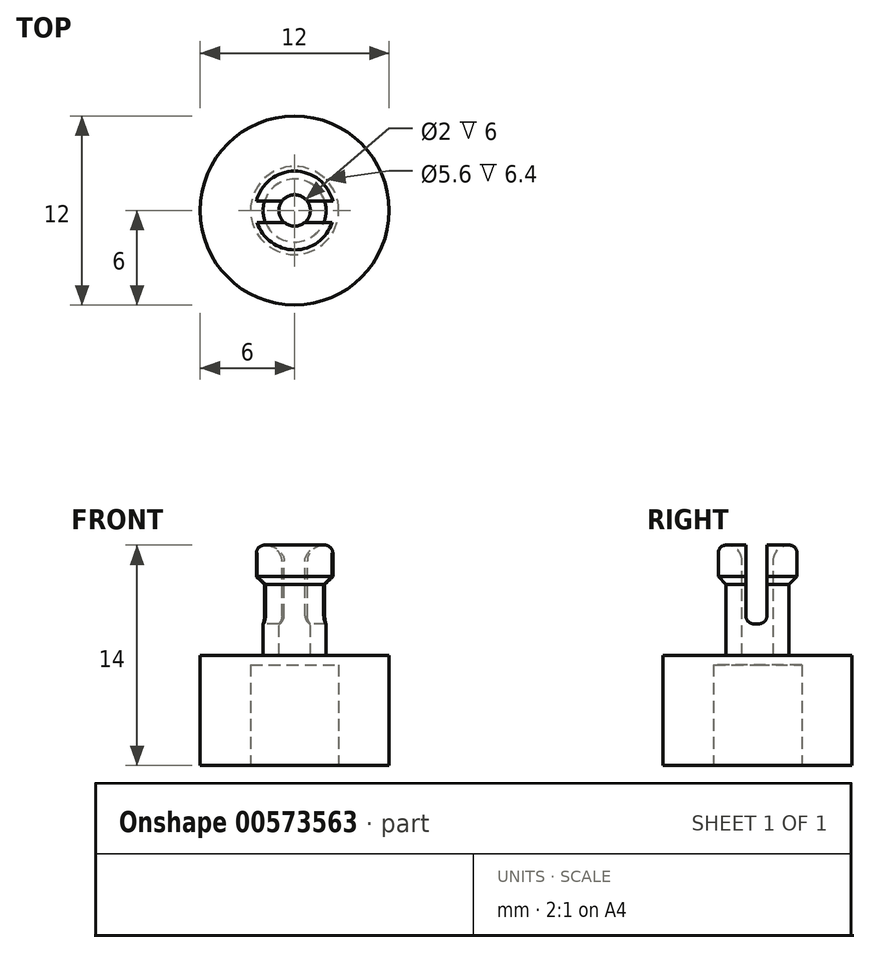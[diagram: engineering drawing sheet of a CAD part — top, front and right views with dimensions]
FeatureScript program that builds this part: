
annotation { "Feature Type Name" : "Feature", "Feature Type Description" : "" }
export const myFeature = defineFeature(function(context is Context, id is Id, definition is map)
    precondition{}
    {
        {
            var Q0;
            Q0=qCreatedBy(makeId("Right.planeOp"),FACE);
            var sketch = newSketch(context, id + "F0", { "sketchPlane" : qUnion([Q0])});
            skLineSegment(sketch, "E0", {"start": v(0, 0) * mm, "end": v(-6, 0) * mm});
            skLineSegment(sketch, "E1", {"start": v(-6, 0) * mm, "end": v(-6, 12) * mm});
            skLineSegment(sketch, "E2", {"start": v(-6, 12) * mm, "end": v(-2, 12) * mm});
            skPoint(sketch, "E3.end.orphan", {"position": v(0, 12) * mm});
            skLineSegment(sketch, "E4", {"start": v(-2, 12) * mm, "end": v(-2, 16) * mm});
            skLineSegment(sketch, "E5", {"start": v(-2, 19) * mm, "end": v(-1, 19) * mm});
            skLineSegment(sketch, "E6", {"start": v(0, 12) * mm, "end": v(0, 0) * mm});
            skLineSegment(sketch, "E7", {"start": v(-2, 16) * mm, "end": v(-2.5, 16) * mm});
            skLineSegment(sketch, "E8", {"start": v(-2.5, 16) * mm, "end": v(-2.5, 19) * mm});
            skLineSegment(sketch, "E9", {"start": v(-2.5, 19) * mm, "end": v(-2, 19) * mm});
            skLineSegment(sketch, "E10", {"start": v(0, 12) * mm, "end": v(-1, 12) * mm});
            skLineSegment(sketch, "E11", {"start": v(-1, 12) * mm, "end": v(-1, 16) * mm});
            skLineSegment(sketch, "E12", {"start": v(-1, 16) * mm, "end": v(-1, 19) * mm});
            skPoint(sketch, "E13.orphan", {"position": v(0, 19) * mm});
            skSolve(sketch);
        }
        {
            var Q0;
            Q0 = qSketchRegion(id + "F0", true);
            var Q1;
            Q1=sQuery(id+"F0.wireOp",EDGE,"E6");
            revolve(context, id + "F1", {"entities" : qUnion([Q0]), "axis" : qUnion([Q1]), "revolveType" : RevolveType.FULL});
        }
        {
            var Q0;
            Q0=makeQuery(id+"F1.opRevolve","SWEPT_FACE",FACE,{"disambiguationData":[OSD([sQuery(id+"F0.wireOp",EDGE,"E5"),sQuery(id+"F0.wireOp",EDGE,"E9")])]});
            var sketch = newSketch(context, id + "F2", { "sketchPlane" : qUnion([Q0])});
            skLineSegment(sketch, "E14", {"start": v(6.48, 0.6) * mm, "end": v(-2.43, 0.6) * mm});
            skLineSegment(sketch, "E15", {"start": v(-2.43, 0.6) * mm, "end": v(-2.63, 0.6) * mm});
            skLineSegment(sketch, "E16", {"start": v(-2.63, 0.6) * mm, "end": v(-2.63, -0.25) * mm});
            skLineSegment(sketch, "E17", {"start": v(6.6, -0.25) * mm, "end": v(6.6, 0.6) * mm});
            skLineSegment(sketch, "E18", {"start": v(6.6, 0.6) * mm, "end": v(2.43, 0.6) * mm});
            skLineSegment(sketch, "E19.MirrorCS", {"start": v(-4.62, -0.56) * mm, "end": v(-4.62, 0) * mm});
            skLineSegment(sketch, "E20.MirrorCS", {"start": v(4.46, -0.75) * mm, "end": v(-4.5, -0.75) * mm});
            skLineSegment(sketch, "E21.MirrorCS", {"start": v(-4.47, -0.56) * mm, "end": v(-4.62, -0.56) * mm});
            skLineSegment(sketch, "E22.MirrorCS", {"start": v(4.61, 0) * mm, "end": v(4.61, -0.56) * mm});
            skLineSegment(sketch, "E23.MirrorCS", {"start": v(4.61, -0.56) * mm, "end": v(4.47, -0.56) * mm});
            skPoint(sketch, "E24.end.orphan", {"position": v(-2.43, -0.25) * mm});
            skPoint(sketch, "E25.orphan", {"position": v(-4.62, 0) * mm});
            skPoint(sketch, "E26.MirrorCS.end.orphan", {"position": v(-4.47, 0) * mm});
            skPoint(sketch, "E26.MirrorCS.start.orphan", {"position": v(-2.5, 0) * mm});
            skPoint(sketch, "E27.start.orphan", {"position": v(2.49, -0.25) * mm});
            skSolve(sketch);
        }
        {
            var Q0;
            {var subQ0=sQuery(id+"F2.wireOp",EDGE,"E14");var subQ3=makeQuery(id+"F1.opRevolve","SWEPT_EDGE",EDGE,{"disambiguationData":[OSD([sQuery(id+"F0.wireOp",EDGE,"E5"),sQuery(id+"F0.wireOp",EDGE,"E12")])]});var subQ4=makeQuery(id+"F2.imprint","INTERSECT",VERTEX,{"disambiguationData":[OD(1.0)],"derivedFrom":[subQ3,subQ0]});Q0=makeQuery(id+"F2.imprint","IMPRINT",FACE,{"disambiguationData":[TD([[makeQuery(id+"F2.imprint","IMPRINT",EDGE,{"disambiguationData":[TD([[subQ4,-1.0]])],"derivedFrom":subQ0}),1.0]])]});}
            var Q1;
            {var subQ0=sQuery(id+"F2.wireOp",EDGE,"E14");var subQ1=makeQuery(id+"F1.opRevolve","SWEPT_EDGE",EDGE,{"disambiguationData":[OSD([sQuery(id+"F0.wireOp",EDGE,"E5"),sQuery(id+"F0.wireOp",EDGE,"E12")])]});var subQ2=makeQuery(id+"F2.imprint","INTERSECT",VERTEX,{"disambiguationData":[OD(0.0)],"derivedFrom":[subQ1,subQ0]});Q1=makeQuery(id+"F2.imprint","IMPRINT",FACE,{"disambiguationData":[TD([[makeQuery(id+"F2.imprint","IMPRINT",EDGE,{"disambiguationData":[TD([[subQ2,-1.0]])],"derivedFrom":subQ0}),1.0]])]});}
            var Q2;
            {var subQ0=sQuery(id+"F2.wireOp",EDGE,"E14");var subQ3=makeQuery(id+"F1.opRevolve","SWEPT_EDGE",EDGE,{"disambiguationData":[OSD([sQuery(id+"F0.wireOp",EDGE,"E5"),sQuery(id+"F0.wireOp",EDGE,"E12")])]});var subQ4=makeQuery(id+"F2.imprint","INTERSECT",VERTEX,{"disambiguationData":[OD(0.0)],"derivedFrom":[subQ3,subQ0]});Q2=makeQuery(id+"F2.imprint","IMPRINT",FACE,{"disambiguationData":[TD([[makeQuery(id+"F2.imprint","IMPRINT",EDGE,{"disambiguationData":[TD([[subQ4,1.0]])],"derivedFrom":subQ0}),1.0]])]});}
            extrude(context, id + "F3", {"entities" : qUnion([Q0, Q1, Q2]), "operationType" : NewBodyOperationType.REMOVE, "oppositeDirection" : true, "depth" : 5 * mm, "offsetDistance" : 25 * mm});
        }
        {
            var Q0;
            {var subQ0=sQuery(id+"F0.wireOp",EDGE,"E7");var subQ1=sQuery(id+"F0.wireOp",EDGE,"E8");Q0=makeQuery(id+"F3.boolean.opBoolean","SPLIT",EDGE,{"disambiguationData":[TD([makeQuery(id+"F3.opExtrude","SWEPT_FACE",FACE,{"disambiguationData":[OSD([sQuery(id+"F2.wireOp",EDGE,"E14")])]})])],"derivedFrom":makeQuery(id+"F1.opRevolve","SWEPT_EDGE",EDGE,{"disambiguationData":[OSD([subQ0,subQ1])]})});}
            var Q1;
            {var subQ0=sQuery(id+"F0.wireOp",EDGE,"E7");var subQ1=sQuery(id+"F0.wireOp",EDGE,"E8");Q1=makeQuery(id+"F3.boolean.opBoolean","SPLIT",EDGE,{"disambiguationData":[TD([makeQuery(id+"F3.opExtrude","SWEPT_FACE",FACE,{"disambiguationData":[OSD([sQuery(id+"F2.wireOp",EDGE,"E20.MirrorCS")])]})])],"derivedFrom":makeQuery(id+"F1.opRevolve","SWEPT_EDGE",EDGE,{"disambiguationData":[OSD([subQ0,subQ1])]})});}
            chamfer(context, id + "F4", {"entities" : qUnion([Q0, Q1]), "width" : 1 * mm, "tangentPropagation" : true});
        }
        {
            var Q0;
            Q0=makeQuery(id+"F1.opRevolve","SWEPT_EDGE",EDGE,{"disambiguationData":[OSD([sQuery(id+"F0.wireOp",EDGE,"E0"),sQuery(id+"F0.wireOp",EDGE,"E1")])]});
            chamfer(context, id + "F5", {"entities" : qUnion([Q0]), "width" : 1 * mm, "tangentPropagation" : true});
        }
        {
            var Q0;
            {var subQ0=sQuery(id+"F0.wireOp",EDGE,"E5");var subQ1=sQuery(id+"F0.wireOp",EDGE,"E12");Q0=makeQuery(id+"F3.boolean.opBoolean","SPLIT",EDGE,{"disambiguationData":[TD([makeQuery(id+"F3.opExtrude","SWEPT_FACE",FACE,{"disambiguationData":[OSD([sQuery(id+"F2.wireOp",EDGE,"E14")])]})])],"derivedFrom":makeQuery(id+"F1.opRevolve","SWEPT_EDGE",EDGE,{"disambiguationData":[OSD([subQ0,subQ1])]})});}
            var Q1;
            {var subQ0=sQuery(id+"F0.wireOp",EDGE,"E5");var subQ1=sQuery(id+"F0.wireOp",EDGE,"E12");Q1=makeQuery(id+"F3.boolean.opBoolean","SPLIT",EDGE,{"disambiguationData":[TD([makeQuery(id+"F3.opExtrude","SWEPT_FACE",FACE,{"disambiguationData":[OSD([sQuery(id+"F2.wireOp",EDGE,"E20.MirrorCS")])]})])],"derivedFrom":makeQuery(id+"F1.opRevolve","SWEPT_EDGE",EDGE,{"disambiguationData":[OSD([subQ0,subQ1])]})});}
            fillet(context, id + "F6", {"entities" : qUnion([Q0, Q1]), "radius" : 1 * mm, "tangentPropagation" : true, "allowEdgeOverflow" : false});
        }
        {
            var Q0;
            {var subQ0=sQuery(id+"F0.wireOp",EDGE,"E9");var subQ1=sQuery(id+"F0.wireOp",EDGE,"E8");Q0=makeQuery(id+"F3.boolean.opBoolean","SPLIT",EDGE,{"disambiguationData":[TD([makeQuery(id+"F3.opExtrude","SWEPT_FACE",FACE,{"disambiguationData":[OSD([sQuery(id+"F2.wireOp",EDGE,"E20.MirrorCS")])]})])],"derivedFrom":makeQuery(id+"F1.opRevolve","SWEPT_EDGE",EDGE,{"disambiguationData":[OSD([subQ1,subQ0])]})});}
            var Q1;
            {var subQ0=sQuery(id+"F0.wireOp",EDGE,"E9");var subQ1=sQuery(id+"F0.wireOp",EDGE,"E8");Q1=makeQuery(id+"F3.boolean.opBoolean","SPLIT",EDGE,{"disambiguationData":[TD([makeQuery(id+"F3.opExtrude","SWEPT_FACE",FACE,{"disambiguationData":[OSD([sQuery(id+"F2.wireOp",EDGE,"E14")])]})])],"derivedFrom":makeQuery(id+"F1.opRevolve","SWEPT_EDGE",EDGE,{"disambiguationData":[OSD([subQ1,subQ0])]})});}
            fillet(context, id + "F7", {"entities" : qUnion([Q0, Q1]), "radius" : .5 * mm, "tangentPropagation" : true, "allowEdgeOverflow" : false});
        }
        {
            var Q0;
            Q0=makeQuery(id+"F3.boolean.opBoolean","COPY",EDGE,{"disambiguationData":[OD(0.0)],"derivedFrom":makeQuery(id+"F3.opExtrude","CAP_EDGE",EDGE,{"disambiguationData":[OSD([sQuery(id+"F2.wireOp",EDGE,"E20.MirrorCS")])],"isStart":false})});
            var Q1;
            Q1=makeQuery(id+"F3.boolean.opBoolean","COPY",EDGE,{"disambiguationData":[OD(0.0)],"derivedFrom":makeQuery(id+"F3.opExtrude","CAP_EDGE",EDGE,{"disambiguationData":[OSD([sQuery(id+"F2.wireOp",EDGE,"E14")])],"isStart":false})});
            var Q2;
            Q2=makeQuery(id+"F3.boolean.opBoolean","COPY",EDGE,{"disambiguationData":[OD(1.0)],"derivedFrom":makeQuery(id+"F3.opExtrude","CAP_EDGE",EDGE,{"disambiguationData":[OSD([sQuery(id+"F2.wireOp",EDGE,"E20.MirrorCS")])],"isStart":false})});
            var Q3;
            Q3=makeQuery(id+"F3.boolean.opBoolean","COPY",EDGE,{"disambiguationData":[OD(1.0)],"derivedFrom":makeQuery(id+"F3.opExtrude","CAP_EDGE",EDGE,{"disambiguationData":[OSD([sQuery(id+"F2.wireOp",EDGE,"E14")])],"isStart":false})});
            fillet(context, id + "F8", {"entities" : qUnion([Q0, Q1, Q2, Q3]), "radius" : .5 * mm, "tangentPropagation" : true, "allowEdgeOverflow" : false});
        }
        {
            var Q0;
            Q0=makeQuery(id+"F1.opRevolve","SWEPT_FACE",FACE,{"disambiguationData":[OSD([sQuery(id+"F0.wireOp",EDGE,"E0")])]});
            var sketch = newSketch(context, id + "F9", { "sketchPlane" : qUnion([Q0])});
            skLineSegment(sketch, "E28.bottom", {"start": v(11.32, 9.5) * mm, "end": v(-9.31, 9.5) * mm});
            skLineSegment(sketch, "E28.top", {"start": v(11.32, -10.4) * mm, "end": v(-9.31, -10.4) * mm});
            skLineSegment(sketch, "E28.left", {"start": v(11.32, 9.5) * mm, "end": v(11.32, -10.4) * mm});
            skLineSegment(sketch, "E28.right", {"start": v(-9.31, 9.5) * mm, "end": v(-9.31, -10.4) * mm});
            skSolve(sketch);
        }
        {
            var Q0;
            Q0=makeQuery(id+"F9.imprint","IMPRINT",FACE,{"disambiguationData":[TD([[makeQuery(id+"F9.imprint","IMPRINT",EDGE,{"derivedFrom":sQuery(id+"F9.wireOp",EDGE,"E28.bottom")}),1.0]])]});
            var Q1;
            {var subQ0=sQuery(id+"F0.wireOp",EDGE,"E0");Q1=makeQuery(id+"F9.imprint","IMPRINT",FACE,{"disambiguationData":[TD([[makeQuery(id+"F9.imprint","IMPRINT",EDGE,{"derivedFrom":makeQuery(id+"F5.opChamfer","BLEND_EDGE",EDGE,{"blendedFrom":[makeQuery(id+"F1.opRevolve","SWEPT_EDGE",EDGE,{"disambiguationData":[OSD([subQ0,sQuery(id+"F0.wireOp",EDGE,"E1")])]}),makeQuery(id+"F1.opRevolve","SWEPT_FACE",FACE,{"disambiguationData":[OSD([subQ0])]})],"blendedInto":[makeQuery(id+"F1.opRevolve","SWEPT_FACE",FACE,{"disambiguationData":[OSD([subQ0])]})]})}),1.0]])]});}
            extrude(context, id + "F10", {"entities" : qUnion([Q0, Q1]), "operationType" : NewBodyOperationType.REMOVE, "oppositeDirection" : true, "depth" : 5 * mm, "offsetDistance" : 25 * mm});
        }
        {
            var Q0;
            Q0=makeQuery(id+"F10.boolean.opBoolean","COPY",FACE,{"derivedFrom":makeQuery(id+"F10.opExtrude","CAP_FACE",FACE,{"disambiguationData":[OSD([sQuery(id+"F9.wireOp",EDGE,"E28.bottom"),sQuery(id+"F9.wireOp",EDGE,"E28.top"),sQuery(id+"F9.wireOp",EDGE,"E28.left"),sQuery(id+"F9.wireOp",EDGE,"E28.right")])],"isStart":false})});
            var sketch = newSketch(context, id + "F11", { "sketchPlane" : qUnion([Q0])});
            skCircle(sketch, "E29", {"center": v(0, 0) * mm, "radius": 2.8 * mm});
            skSolve(sketch);
        }
        {
            var Q0;
            Q0=makeQuery(id+"F11.imprint","IMPRINT",FACE,{"disambiguationData":[TD([[makeQuery(id+"F11.imprint","IMPRINT",EDGE,{"derivedFrom":sQuery(id+"F11.wireOp",EDGE,"E29")}),1.0]])]});
            extrude(context, id + "F12", {"entities" : qUnion([Q0]), "operationType" : NewBodyOperationType.REMOVE, "oppositeDirection" : true, "depth" : 6.4 * mm, "offsetDistance" : 25 * mm});
        }
    });
